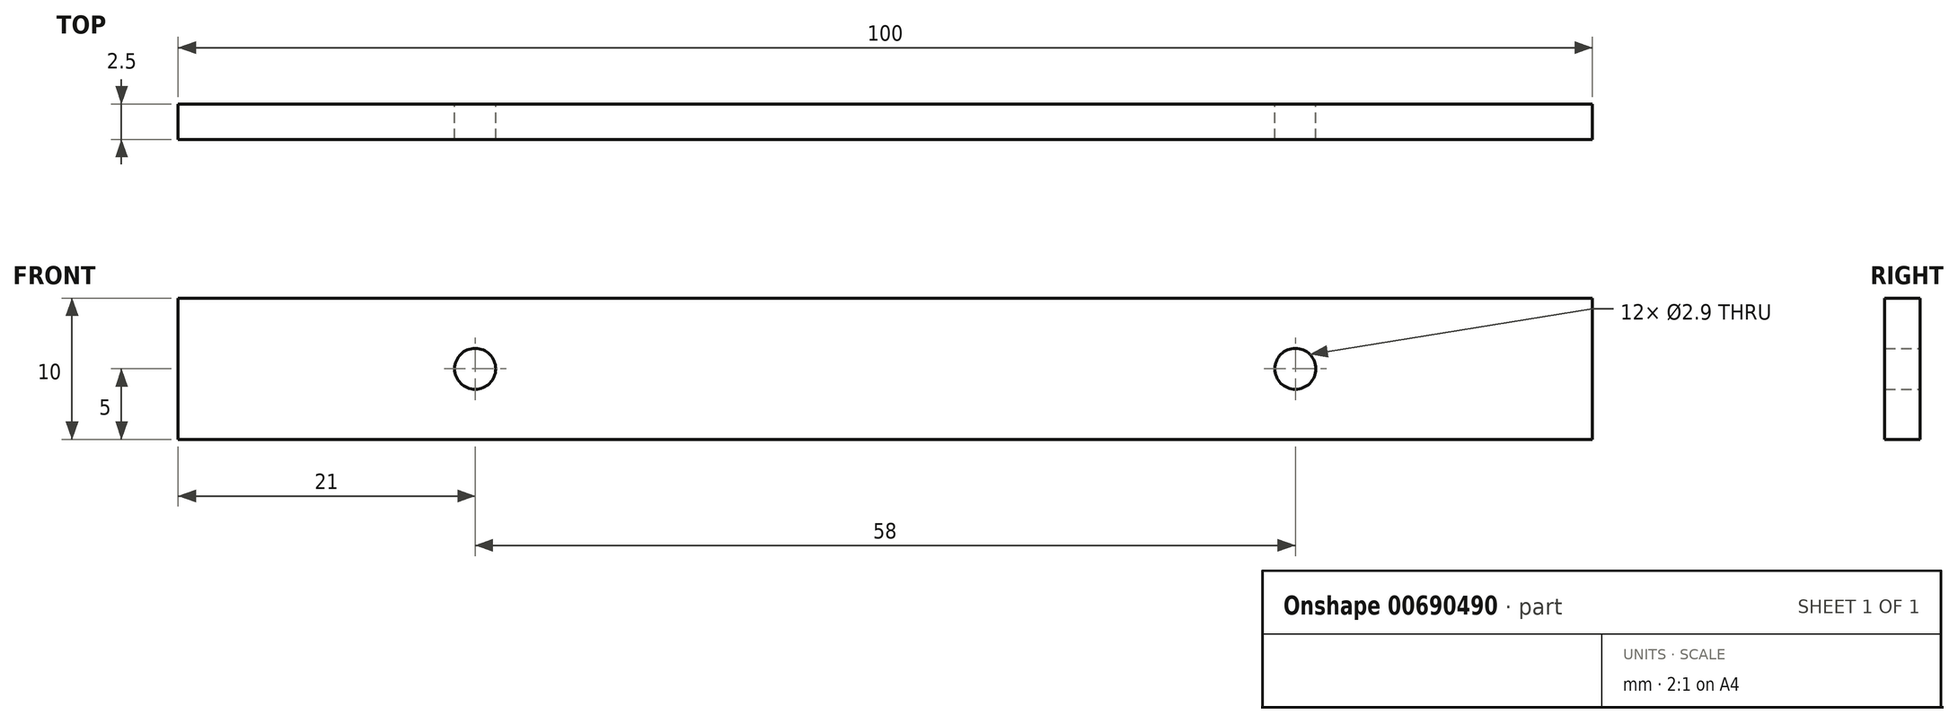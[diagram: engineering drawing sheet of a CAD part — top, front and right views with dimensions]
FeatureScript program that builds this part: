
annotation { "Feature Type Name" : "Feature", "Feature Type Description" : "" }
export const myFeature = defineFeature(function(context is Context, id is Id, definition is map)
    precondition{}
    {
        {
            var Q0;
            Q0=qCreatedBy(makeId("Front.planeOp"),FACE);
            var sketch = newSketch(context, id + "F0", { "sketchPlane" : qUnion([Q0])});
            skLineSegment(sketch, "E0.bottom", {"start": v(-50, 5) * mm, "end": v(50, 5) * mm});
            skLineSegment(sketch, "E0.top", {"start": v(-50, -5) * mm, "end": v(50, -5) * mm});
            skLineSegment(sketch, "E0.left", {"start": v(-50, 5) * mm, "end": v(-50, -5) * mm});
            skLineSegment(sketch, "E0.right", {"start": v(50, 5) * mm, "end": v(50, -5) * mm});
            skCircle(sketch, "E1", {"center": v(-29, 0) * mm, "radius": 1.45 * mm});
            skCircle(sketch, "E2.MirrorC", {"center": v(29, 0) * mm, "radius": 1.45 * mm});
            skSolve(sketch);
        }
        {
            var Q0;
            Q0 = qSketchRegion(id + "F0", true);
            extrude(context, id + "F1", {"entities" : qUnion([Q0]), "depth" : 2.5 * mm, "offsetDistance" : 25 * mm});
        }
    });
